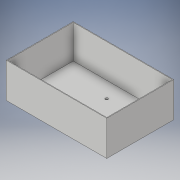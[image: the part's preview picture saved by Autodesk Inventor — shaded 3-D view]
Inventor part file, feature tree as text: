
AUTODESK INVENTOR PART (.ipt)
format: ipt  version: 2018 (Build 220112000, 112)  size: 113,664 bytes
history: native  units: in
note: dims shown in document units (in); Inventor stores cm internally (conversion verified against a paired STEP export)
features: extrude x3, sketch x3
ambient origin geometry x8: Origin, YZ Plane, XZ Plane, XY Plane, X Axis, Y Axis, Z Axis, Center Point
bodies: Solid1 (feature_tree)
feature tree (6):
  extrude  "Extrusion1"  Depth=4.0in
  extrude  "Extrusion2"  Depth=5.92in
  extrude  "Extrusion3"  Depth=2.0in TaperAngle=0.0deg
  sketch  "Sketch1"  dims[d0=6.0in d1=4.0in]
  sketch  "Sketch2"  dims[d2=0.08in d3=0.0in d4=5.92in]
  sketch  "Sketch3"  dims[d5=3.92in d6=2.0in d7=0.0in d10=0.164in d11=0.164in d12=0.0in d13=0.0in]
